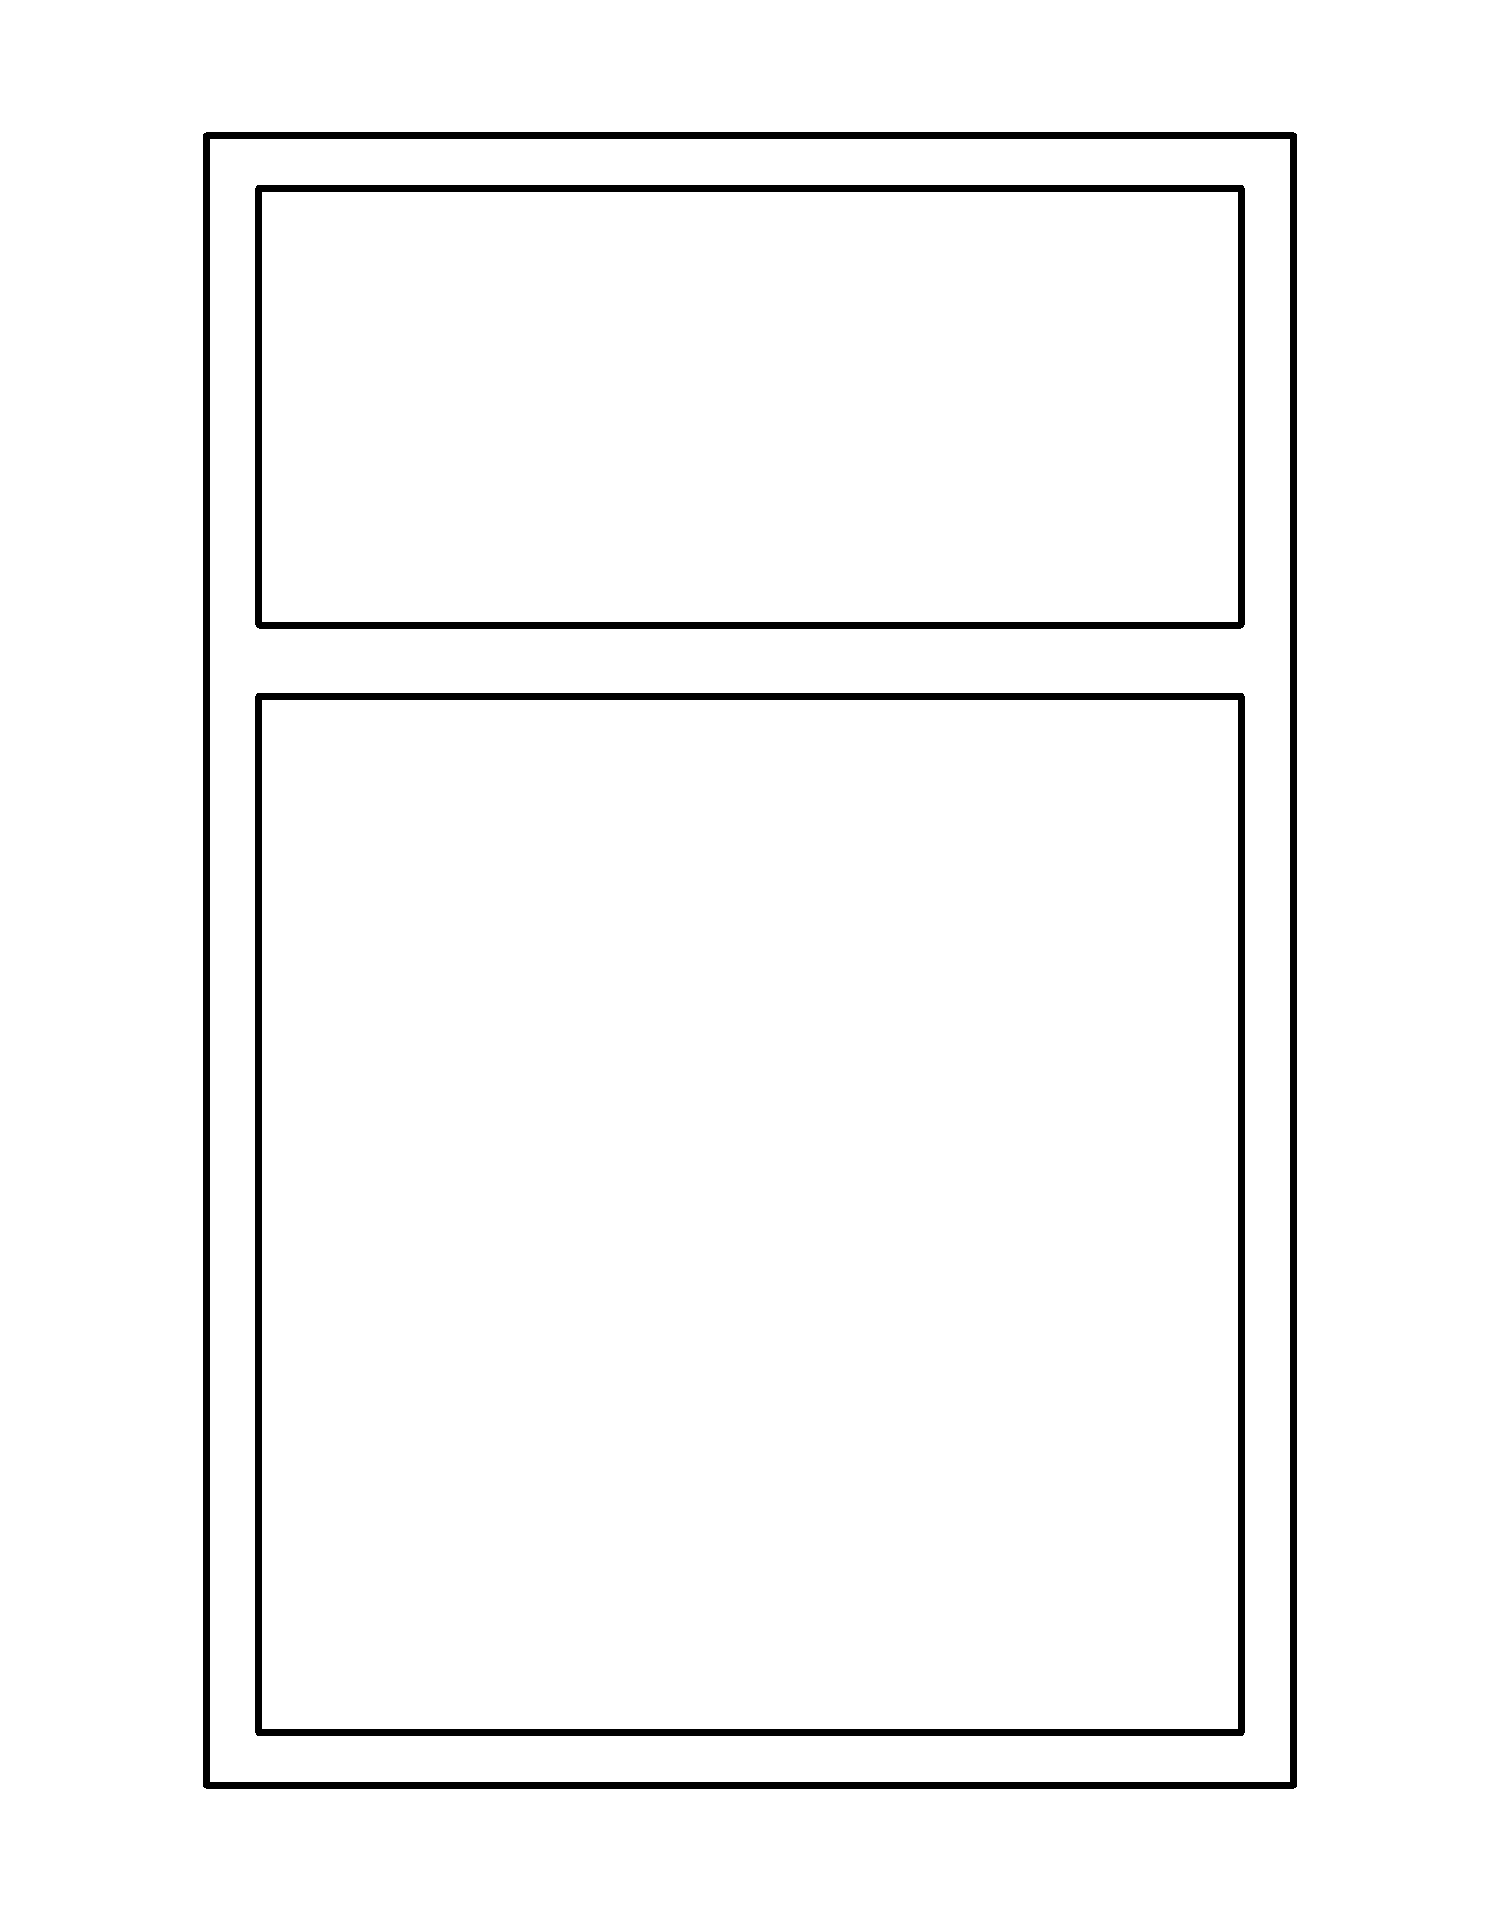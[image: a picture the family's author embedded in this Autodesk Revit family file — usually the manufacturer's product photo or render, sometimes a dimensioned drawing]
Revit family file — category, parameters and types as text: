
# Revit family: Окно.Alumark_с фрамугой_S44
name_source: partatom
category: Окна
revit_build: Autodesk Revit 2017 (Build: 20171027_0315(x64)
units: mm (PartAtom-declared; Revit-internal decimal feet)

## family parameters
Всегда вертикально = Да
Заголовок OmniClass = Windows
Номер OmniClass = 23.30.20.00
Общий = Нет
Основа = Стена
При загрузке вырезать с полостями = Нет
Точка расчета площади = Нет

## types (2) — shared parameters
#_рамы = 1000000
ADSK_Завод-изготовитель = ТБМ
ADSK_Наименование = ОАК (Профиль рамы 44/26 мм) СПО (Обычный стеклопакет 16 мм)
ADSK_Обозначение = ГОСТ 21519-2003
URL = http://www.tbm.ru
sp_energy = Энергосберегающие стекла
sp_gaz = Заполненный газом
sp_standart = Обычный стеклопакет
Автоматический подбор рамы и створки = Да
Аналитическая конструкция = Окна с одинарным остеклением - для жилых зданий
Высота подоконника по умолчанию = 900 мм
Высота створки сверху = 500 мм
Замыкание стены = По основе
Заполнение стеклопакета = Обычный стеклопакет
Изготовитель = ТБМ
Изображение типоразмера = схема_однопольное_фрамуга_сверху.png
Коэффициент теплопередачи (U) = 5.7361 Вт/(м²·K)
Коэффициент теплопритока от солнечного излучения = 0.86
Материал отлива = <По категории>
Материал подоконника = <По категории>
Материал рамы/створки = <По категории>
Материал стекла = <По категории>
Материал фурнитуры = <По категории>
Описание = Окно Проем ТБМ
Примерная высота = 1560 мм
Примерная ширина = 760 мм
Пропускание видимого света = 0.9
Разработчик = ООО ПРОРУБИМ
Разработчик (телефон) = +7(495)649-85-43
Створка сверху = Окна.Alumark_створка_двупольная (S44) : Глухая
ТБМ_Артикул_Импост = ALM244301
ТБМ_Артикул_Клей = KMR0014
ТБМ_Артикул_Подкладка под СП = ALM740307
ТБМ_Артикул_Рама = ALM244101
ТБМ_Артикул_Распорный штифт = ALM885010
ТБМ_Артикул_Угловой соединитель рамы = ALM420011
ТБМ_Артикул_Уголок выравнивающий = ALM744014
ТБМ_Артикул_Уплотнитель внутренний = ALM770207
ТБМ_Артикул_Уплотнитель наружный = ALM770004
ТБМ_Артикул_Штапик = ALM244013
ТБМ_Длина_Импост = 720 мм
ТБМ_Длина_Рама = 4640 мм
ТБМ_Количество_Подкладка под СП = 12
ТБМ_Количество_Угловой соединитель рамы = 4
ТБМ_Расход_Клей = 28
ТБМ_Соответствие рекомендациям = Размеры окна соответствует рекомендациям компании ТБМ
ТБМ_Стеклопакет_Высота 1 = 434 мм
ТБМ_Стеклопакет_Ширина 1 = 694 мм
Термостойкость = 0.1743 (м²·K)/Вт
Тип рамы = Рама оконная : 44/26 мм (ALM244101)
Тип створки = Створка оконная : 32/43 мм (ALM244201)
Тип стеклопакета = 16мм 1-камерный
глухая_створка = Окна.Alumark_створка_двупольная (S44) : Глухая
импост_ширина = 62 мм
номер профиля = 1000101
обозначение_проема_высота = 260 мм
обозначение_проема_ширина = 127 мм
профиль створки_ширина = 43 мм
размер_X = 43 мм
размер_Y = 20 мм
размер_Z = 26 мм
рама_тип-1 = Рама оконная : 44/26 мм (ALM244101)
рама_тип-2 = Рама оконная : 60/42 мм (ALM244102)
рама_толщина = 44 мм
рама_ширина = 44 мм
сп_16_мм = 16мм 1-камерный
сп_24_мм = 24мм 1-камерный
створка_внизу_высота = 985 мм
створка_высота = 1472 мм
створка_сверху_высота = 425 мм
створка_тип-1 = Створка оконная : 32/43 мм (ALM244201)
створка_тип-2 = Створка оконная : 48/59 мм (ALM244202)
створка_ширина = 672 мм
таблица выбора = Каталог_окна_S44
штапик_толщина = 28 мм
штапик_ширина = 18 мм
zero-valued in all types: #_створки, профиль_створка_сверху_длина

## per-type parameters (varying)
| type | Створка внизу | ТБМ_Артикул_Отлив | ТБМ_Артикул_Створка | ТБМ_Артикул_Угловой соединитель створки | ТБМ_Артикул_Уголок жесткости | ТБМ_Артикул_Уплотнитель притвора | ТБМ_Длина_Отлив | ТБМ_Длина_Створка | ТБМ_Длина_Уплотнитель внутренний | ТБМ_Длина_Уплотнитель наружный | ТБМ_Длина_Уплотнитель притвора | ТБМ_Длина_Штапик | ТБМ_Количество_Распорный штифт | ТБМ_Количество_Угловой соединитель створки | ТБМ_Количество_Уголок выравнивающий | ТБМ_Количество_Уголок жесткости | ТБМ_Площадь стеклопакета | ТБМ_Стеклопакет_Высота 2 | ТБМ_Стеклопакет_Ширина 2 | профиль_створка_внизу_длина |
| 760х1560 (правое-откидное) | Окна.Alumark_створка_двупольная (S44) : Правая-откидная | ALM460035-1.07 | ALM244201 | ALM420011 | ALM744501 | ALM770001 | -26 мм | 3480 мм | 8120 мм | 8120 мм | 3480 мм | 5448 мм | 32 | 4 | 8 | 4 | 0.88 м² | 926 мм | 626 мм | 3480 мм |
| 760х1560 (глухое) | Окна.Alumark_створка_двупольная (S44) : Глухая |  |  |  |  |  | 0 мм | 0 мм | 9280 мм | 9280 мм | 0 мм | 5744 мм | 16 | 0 | 4 | 0 | 0.99 м² | 994 мм | 694 мм | 0 мм |
